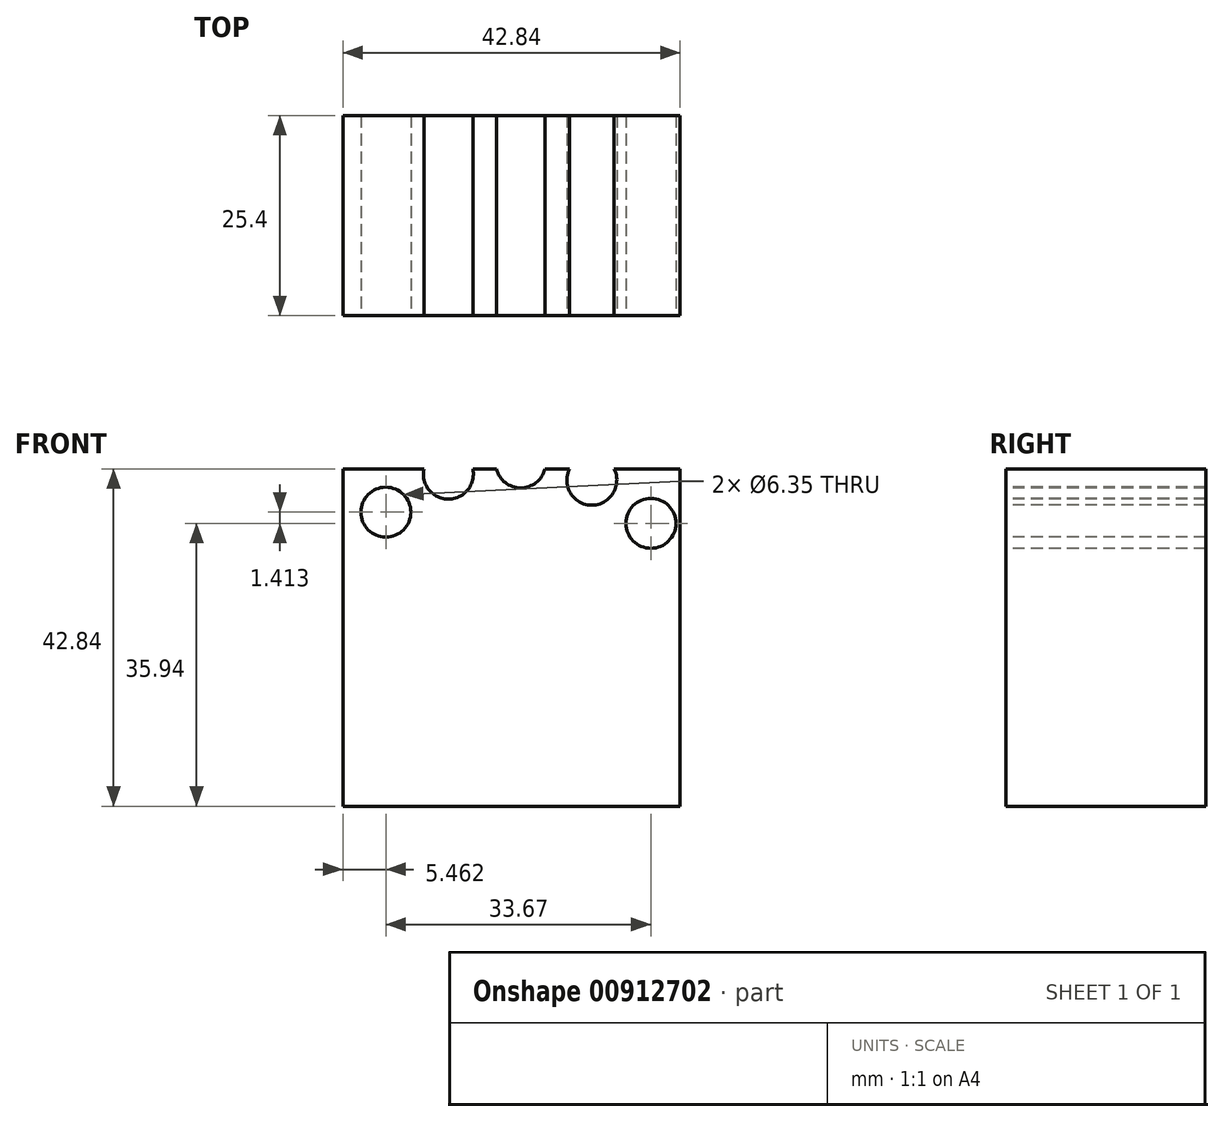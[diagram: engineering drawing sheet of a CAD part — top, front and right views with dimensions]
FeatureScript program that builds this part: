
annotation { "Feature Type Name" : "Feature", "Feature Type Description" : "" }
export const myFeature = defineFeature(function(context is Context, id is Id, definition is map)
    precondition{}
    {
        {
            var Q0;
            Q0=qCreatedBy(makeId("Front.planeOp"),FACE);
            var sketch = newSketch(context, id + "F0", { "sketchPlane" : qUnion([Q0])});
            skLineSegment(sketch, "E0", {"start": v(0, 42.84) * mm, "end": v(0, 0) * mm});
            skLineSegment(sketch, "E1", {"start": v(0, 0) * mm, "end": v(42.84, 0) * mm});
            skLineSegment(sketch, "E2", {"start": v(42.84, 0) * mm, "end": v(42.84, 42.84) * mm});
            skLineSegment(sketch, "E3", {"start": v(42.84, 42.84) * mm, "end": v(0, 42.84) * mm});
            skSolve(sketch);
        }
        {
            var Q0;
            Q0 = qSketchRegion(id + "F0", true);
            extrude(context, id + "F1", {"entities" : qUnion([Q0]), "depth" : 25.4 * mm, "offsetDistance" : 25.4 * mm});
        }
        {
            var Q0;
            Q0=makeQuery(id+"F1.opExtrude","CAP_FACE",FACE,{"disambiguationData":[OSD([sQuery(id+"F0.wireOp",EDGE,"E0"),sQuery(id+"F0.wireOp",EDGE,"E1"),sQuery(id+"F0.wireOp",EDGE,"E2"),sQuery(id+"F0.wireOp",EDGE,"E3")])],"isStart":false});
            var sketch = newSketch(context, id + "F2", { "sketchPlane" : qUnion([Q0])});
            skCircle(sketch, "E4", {"center": v(5.46, 37.35) * mm, "radius": 2.2 * mm});
            skCircle(sketch, "E5.1.0", {"center": v(13.4, 42.19) * mm, "radius": 2.2 * mm});
            skCircle(sketch, "E5.2.0", {"center": v(22.59, 43.62) * mm, "radius": 2.2 * mm});
            skCircle(sketch, "E5.3.0", {"center": v(31.62, 41.43) * mm, "radius": 2.2 * mm});
            skCircle(sketch, "E5.4.0", {"center": v(39.13, 35.94) * mm, "radius": 2.2 * mm});
            skPoint(sketch, "E5.center", {"position": v(21.59, 19.81) * mm});
            skLineSegment(sketch, "E5.anchor1", {"start": v(21.6, 19.81) * mm, "end": v(5.46, 37.35) * mm, "construction": true});
            skLineSegment(sketch, "E5.anchor2", {"start": v(21.59, 19.81) * mm, "end": v(39.13, 35.94) * mm, "construction": true});
            skSolve(sketch);
        }
        {
            var Q0;
            Q0=sQuery(id+"F2.wireOp",VERTEX,"E5.anchor1.end");
            var Q1;
            Q1=sQuery(id+"F2.wireOp",VERTEX,"E5.anchor2.end");
            var Q2;
            Q2=sQuery(id+"F2.wireOp",VERTEX,"E5.3.0.center");
            var Q3;
            Q3=sQuery(id+"F2.wireOp",VERTEX,"E5.2.0.center");
            var Q4;
            Q4=sQuery(id+"F2.wireOp",VERTEX,"E5.1.0.center");
            var Q5;
            Q5=makeQuery(id+"F1.opExtrude","SWEPT_BODY",BODY,{"disambiguationData":[OSD([sQuery(id+"F0.wireOp",EDGE,"E0"),sQuery(id+"F0.wireOp",EDGE,"E1"),sQuery(id+"F0.wireOp",EDGE,"E2"),sQuery(id+"F0.wireOp",EDGE,"E3")])]});
            hole(context, id + "F3", {"style" : HoleStyle.SIMPLE, "endStyle" : HoleEndStyle.THROUGH, "holeDiameter" : 6.35 * mm, "majorDiameter" : 6.35 * mm, "isTappedThrough" : true, "tappedDepth" : 12.7 * mm, "tapClearance" : 3, "locations" : qUnion([Q0, Q1, Q2, Q3, Q4]), "scope" : qUnion([Q5])});
        }
    });
